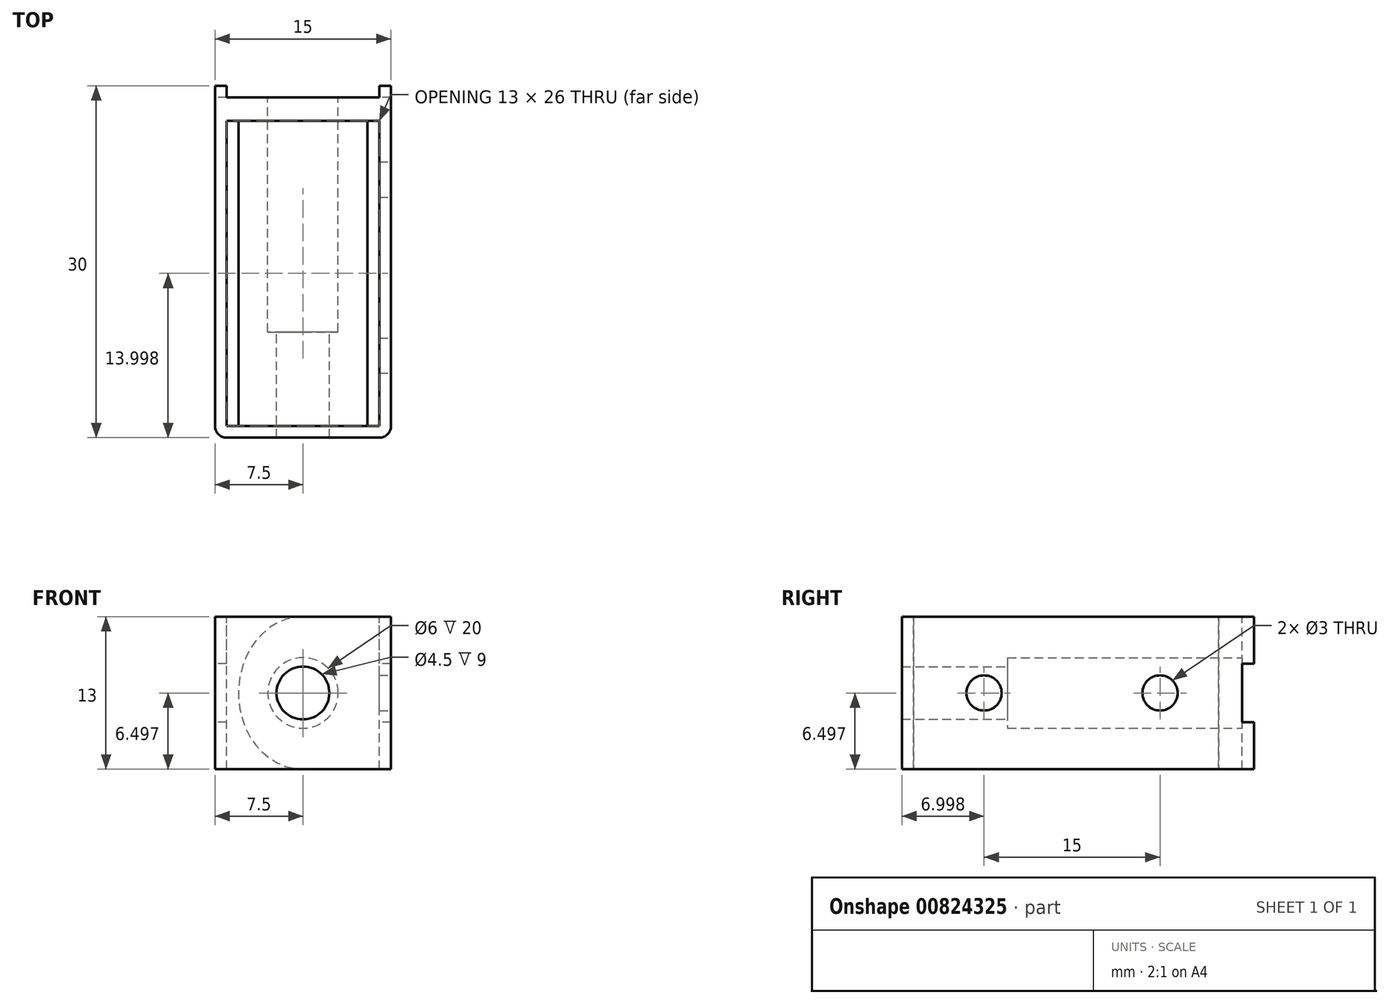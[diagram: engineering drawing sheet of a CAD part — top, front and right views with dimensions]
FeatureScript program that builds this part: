
annotation { "Feature Type Name" : "Feature", "Feature Type Description" : "" }
export const myFeature = defineFeature(function(context is Context, id is Id, definition is map)
    precondition{}
    {
        {
            var Q0;
            Q0=qCreatedBy(makeId("Right.planeOp"),FACE);
            var sketch = newSketch(context, id + "F0", { "sketchPlane" : qUnion([Q0])});
            skLineSegment(sketch, "E0.bottom", {"start": v(-32.8, 20.89) * mm, "end": v(-2.8, 20.89) * mm});
            skLineSegment(sketch, "E0.top", {"start": v(-32.8, 7.89) * mm, "end": v(-2.8, 7.89) * mm});
            skLineSegment(sketch, "E0.left", {"start": v(-32.8, 20.89) * mm, "end": v(-32.8, 7.89) * mm});
            skLineSegment(sketch, "E0.right", {"start": v(-2.8, 20.89) * mm, "end": v(-2.8, 7.89) * mm});
            skSolve(sketch);
        }
        {
            var Q0;
            Q0=makeQuery(id+"F0.imprint","IMPRINT",FACE,{"disambiguationData":[TD([[makeQuery(id+"F0.imprint","IMPRINT",EDGE,{"derivedFrom":sQuery(id+"F0.wireOp",EDGE,"E0.bottom")}),-1.0]])]});
            extrude(context, id + "F1", {"entities" : qUnion([Q0]), "oppositeDirection" : true, "depth" : 15 * mm, "offsetDistance" : 25 * mm});
        }
        {
            var Q0;
            Q0=makeQuery(id+"F1.opExtrude","SWEPT_FACE",FACE,{"disambiguationData":[OSD([sQuery(id+"F0.wireOp",EDGE,"E0.bottom")])]});
            var sketch = newSketch(context, id + "F2", { "sketchPlane" : qUnion([Q0])});
            skLineSegment(sketch, "E1", {"start": v(-1, -31.8) * mm, "end": v(-1, -5.8) * mm});
            skLineSegment(sketch, "E2", {"start": v(-14, -5.8) * mm, "end": v(-14, -31.8) * mm});
            skLineSegment(sketch, "E3", {"start": v(-14, -5.8) * mm, "end": v(-1, -5.8) * mm});
            skLineSegment(sketch, "E4", {"start": v(-14, -31.8) * mm, "end": v(-1, -31.8) * mm});
            skSolve(sketch);
        }
        {
            var Q0;
            Q0 = qSketchRegion(id + "F2", true);
            var Q1;
            Q1=makeQuery(id+"F1.opExtrude","SWEPT_FACE",FACE,{"disambiguationData":[OSD([sQuery(id+"F0.wireOp",EDGE,"E0.top")])]});
            extrude(context, id + "F3", {"entities" : qUnion([Q0]), "operationType" : NewBodyOperationType.REMOVE, "endBound" : BoundingType.UP_TO_SURFACE, "oppositeDirection" : true, "depth" : 25 * mm, "endBoundEntityFace" : qUnion([Q1]), "offsetDistance" : 25 * mm});
        }
        {
            var Q0;
            Q0=makeQuery(id+"F1.opExtrude","CAP_FACE",FACE,{"disambiguationData":[OSD([sQuery(id+"F0.wireOp",EDGE,"E0.bottom"),sQuery(id+"F0.wireOp",EDGE,"E0.top"),sQuery(id+"F0.wireOp",EDGE,"E0.left"),sQuery(id+"F0.wireOp",EDGE,"E0.right")])],"isStart":true});
            var sketch = newSketch(context, id + "F4", { "sketchPlane" : qUnion([Q0])});
            skLineSegment(sketch, "E5.bottom", {"start": v(-25.8, 20.89) * mm, "end": v(-10.8, 20.89) * mm, "construction": true});
            skLineSegment(sketch, "E5.top", {"start": v(-25.8, 7.89) * mm, "end": v(-10.8, 7.89) * mm, "construction": true});
            skLineSegment(sketch, "E5.left", {"start": v(-25.8, 20.89) * mm, "end": v(-25.8, 7.89) * mm, "construction": true});
            skLineSegment(sketch, "E5.right", {"start": v(-10.8, 20.89) * mm, "end": v(-10.8, 7.89) * mm, "construction": true});
            skCircle(sketch, "E6", {"center": v(-25.8, 14.39) * mm, "radius": 1.5 * mm});
            skCircle(sketch, "E7", {"center": v(-10.8, 14.39) * mm, "radius": 1.5 * mm});
            skLineSegment(sketch, "E8", {"start": v(-25.8, 15.89) * mm, "end": v(-10.8, 15.89) * mm, "construction": true});
            skLineSegment(sketch, "E9", {"start": v(-25.8, 12.89) * mm, "end": v(-10.8, 12.89) * mm, "construction": true});
            skSolve(sketch);
        }
        {
            var Q0;
            Q0 = qSketchRegion(id + "F4", true);
            var Q1;
            Q1=makeQuery(id+"F3.boolean.opBoolean","COPY",FACE,{"derivedFrom":makeQuery(id+"F3.opExtrude","SWEPT_FACE",FACE,{"disambiguationData":[OSD([sQuery(id+"F2.wireOp",EDGE,"E1")])]})});
            extrude(context, id + "F5", {"entities" : qUnion([Q0]), "operationType" : NewBodyOperationType.REMOVE, "endBound" : BoundingType.UP_TO_SURFACE, "oppositeDirection" : true, "depth" : 1 * mm, "endBoundEntityFace" : qUnion([Q1]), "offsetDistance" : 25 * mm});
        }
        {
            var Q0;
            Q0=makeQuery(id+"F3.boolean.opBoolean","COPY",FACE,{"derivedFrom":makeQuery(id+"F3.opExtrude","SWEPT_FACE",FACE,{"disambiguationData":[OSD([sQuery(id+"F2.wireOp",EDGE,"E3")])]})});
            var sketch = newSketch(context, id + "F6", { "sketchPlane" : qUnion([Q0])});
            skLineSegment(sketch, "E10.bottom", {"start": v(-0.5, 21.89) * mm, "end": v(-14.5, 21.89) * mm, "construction": true});
            skLineSegment(sketch, "E10.top", {"start": v(-0.5, 6.89) * mm, "end": v(-14.5, 6.89) * mm, "construction": true});
            skLineSegment(sketch, "E10.left", {"start": v(-0.5, 21.89) * mm, "end": v(-0.5, 6.89) * mm, "construction": true});
            skLineSegment(sketch, "E10.right", {"start": v(-14.5, 21.89) * mm, "end": v(-14.5, 6.89) * mm, "construction": true});
            skPoint(sketch, "E10.middle", {"position": v(-7.5, 14.39) * mm});
            skPoint(sketch, "E10.middle.positionSnap0", {"position": v(-1, 14.39) * mm});
            skPoint(sketch, "E10.middle.positionSnap1", {"position": v(-7.5, 20.89) * mm});
            skPoint(sketch, "E10.centerSnap0", {"position": v(-1, 14.39) * mm});
            skPoint(sketch, "E10.centerSnap1", {"position": v(-7.5, 20.89) * mm});
            skLineSegment(sketch, "E11", {"start": v(-7.5, 21.89) * mm, "end": v(-7.5, 6.89) * mm, "construction": true});
            skLineSegment(sketch, "E12", {"start": v(-14.5, 14.39) * mm, "end": v(-0.5, 14.39) * mm, "construction": true});
            skEllipse(sketch, "E13", {"center": v(-7.5, 14.39) * mm, "majorRadius": 6.5 * mm, "minorRadius": 5.5 * mm, "majorAxis": v(0, 1)});
            skSolve(sketch);
        }
        {
            var Q0;
            {var subQ0=sQuery(id+"F6.wireOp",EDGE,"E13");var subQ1=makeQuery(id+"F3.boolean.opBoolean","COPY",EDGE,{"derivedFrom":makeQuery(id+"F3.opExtrude","CAP_EDGE",EDGE,{"disambiguationData":[OSD([sQuery(id+"F2.wireOp",EDGE,"E3")])],"isStart":true})});var subQ2=makeQuery(id+"F6.imprint","INTERSECT",VERTEX,{"disambiguationData":[OD(0.0)],"derivedFrom":[subQ1,subQ0]});Q0=makeQuery(id+"F6.imprint","IMPRINT",FACE,{"disambiguationData":[TD([[makeQuery(id+"F6.imprint","IMPRINT",EDGE,{"disambiguationData":[TD([[subQ2,-1.0]])],"derivedFrom":subQ0}),1.0]])]});}
            var Q1;
            {var subQ0=sQuery(id+"F6.wireOp",EDGE,"E13");var subQ1=makeQuery(id+"F3.boolean.opBoolean","COPY",EDGE,{"derivedFrom":makeQuery(id+"F3.opExtrude","TWEAK_EDGE",EDGE,{"derivedFrom":[makeQuery(id+"F1.opExtrude","SWEPT_FACE",FACE,{"disambiguationData":[OSD([sQuery(id+"F0.wireOp",EDGE,"E0.top")])]}),makeQuery(id+"F2.imprint","IMPRINT",EDGE,{"derivedFrom":sQuery(id+"F2.wireOp",EDGE,"E3")})]})});var subQ2=makeQuery(id+"F6.imprint","INTERSECT",VERTEX,{"disambiguationData":[OD(0.0)],"derivedFrom":[subQ1,subQ0]});Q1=makeQuery(id+"F6.imprint","IMPRINT",FACE,{"disambiguationData":[TD([[makeQuery(id+"F6.imprint","IMPRINT",EDGE,{"disambiguationData":[TD([[subQ2,-1.0]])],"derivedFrom":subQ0}),1.0]])]});}
            var Q2;
            {var subQ0=sQuery(id+"F6.wireOp",EDGE,"E13");var subQ1=makeQuery(id+"F3.boolean.opBoolean","COPY",EDGE,{"derivedFrom":makeQuery(id+"F3.opExtrude","CAP_EDGE",EDGE,{"disambiguationData":[OSD([sQuery(id+"F2.wireOp",EDGE,"E3")])],"isStart":true})});var subQ2=makeQuery(id+"F6.imprint","INTERSECT",VERTEX,{"disambiguationData":[OD(0.0)],"derivedFrom":[subQ1,subQ0]});Q2=makeQuery(id+"F6.imprint","IMPRINT",FACE,{"disambiguationData":[TD([[makeQuery(id+"F6.imprint","IMPRINT",EDGE,{"disambiguationData":[TD([[subQ2,1.0]])],"derivedFrom":subQ0}),1.0]])]});}
            var Q3;
            Q3=makeQuery(id+"F3.boolean.opBoolean","COPY",FACE,{"derivedFrom":makeQuery(id+"F3.opExtrude","SWEPT_FACE",FACE,{"disambiguationData":[OSD([sQuery(id+"F2.wireOp",EDGE,"E4")])]})});
            extrude(context, id + "F7", {"entities" : qUnion([Q0, Q1, Q2]), "operationType" : NewBodyOperationType.ADD, "endBound" : BoundingType.UP_TO_SURFACE, "depth" : 25 * mm, "endBoundEntityFace" : qUnion([Q3]), "offsetDistance" : 25 * mm});
        }
        {
            var Q0;
            Q0=makeQuery(id+"F1.opExtrude","CAP_EDGE",EDGE,{"disambiguationData":[OSD([sQuery(id+"F0.wireOp",EDGE,"E0.left")])],"isStart":false});
            var Q1;
            Q1=makeQuery(id+"F1.opExtrude","CAP_EDGE",EDGE,{"disambiguationData":[OSD([sQuery(id+"F0.wireOp",EDGE,"E0.left")])],"isStart":true});
            fillet(context, id + "F8", {"entities" : qUnion([Q0, Q1]), "radius" : 1 * mm, "tangentPropagation" : true, "allowEdgeOverflow" : false});
        }
        {
            var Q0;
            Q0=makeQuery(id+"F1.opExtrude","SWEPT_FACE",FACE,{"disambiguationData":[OSD([sQuery(id+"F0.wireOp",EDGE,"E0.right")])]});
            var sketch = newSketch(context, id + "F9", { "sketchPlane" : qUnion([Q0])});
            skLineSegment(sketch, "E14.bottom", {"start": v(14, 7.89) * mm, "end": v(1, 7.89) * mm});
            skLineSegment(sketch, "E14.top", {"start": v(14, 20.89) * mm, "end": v(1, 20.89) * mm});
            skLineSegment(sketch, "E14.left", {"start": v(14, 7.89) * mm, "end": v(14, 20.89) * mm});
            skLineSegment(sketch, "E14.right", {"start": v(1, 7.89) * mm, "end": v(1, 20.89) * mm});
            skPoint(sketch, "E14.middle", {"position": v(7.5, 14.39) * mm});
            skPoint(sketch, "E14.middle.positionSnap0", {"position": v(15, 14.39) * mm});
            skPoint(sketch, "E14.middle.positionSnap1", {"position": v(7.5, 20.89) * mm});
            skPoint(sketch, "E14.centerSnap0", {"position": v(15, 14.39) * mm});
            skPoint(sketch, "E14.centerSnap1", {"position": v(7.5, 20.89) * mm});
            skLineSegment(sketch, "E15.bottom", {"start": v(0, 16.89) * mm, "end": v(15, 16.89) * mm});
            skLineSegment(sketch, "E15.top", {"start": v(0, 11.89) * mm, "end": v(15, 11.89) * mm});
            skLineSegment(sketch, "E15.left", {"start": v(0, 16.89) * mm, "end": v(0, 11.89) * mm});
            skLineSegment(sketch, "E15.right", {"start": v(15, 16.89) * mm, "end": v(15, 11.89) * mm});
            skSolve(sketch);
        }
        {
            var Q0;
            Q0 = qSketchRegion(id + "F9", true);
            extrude(context, id + "F10", {"entities" : qUnion([Q0]), "operationType" : NewBodyOperationType.REMOVE, "oppositeDirection" : true, "depth" : 1 * mm, "offsetDistance" : 25 * mm});
        }
        {
            var Q0;
            Q0=makeQuery(id+"F10.boolean.opBoolean","COPY",FACE,{"derivedFrom":makeQuery(id+"F10.opExtrude","CAP_FACE",FACE,{"disambiguationData":[OSD([sQuery(id+"F9.wireOp",EDGE,"E14.bottom"),sQuery(id+"F9.wireOp",EDGE,"E14.top"),sQuery(id+"F9.wireOp",EDGE,"E14.left"),sQuery(id+"F9.wireOp",EDGE,"E14.right"),sQuery(id+"F9.wireOp",EDGE,"E15.bottom"),sQuery(id+"F9.wireOp",EDGE,"E15.top"),sQuery(id+"F9.wireOp",EDGE,"E15.left"),sQuery(id+"F9.wireOp",EDGE,"E15.right")])],"isStart":false})});
            var sketch = newSketch(context, id + "F11", { "sketchPlane" : qUnion([Q0])});
            skCircle(sketch, "E16", {"center": v(7.5, 14.39) * mm, "radius": 3 * mm});
            skPoint(sketch, "E16.centerSnap0", {"position": v(7.5, 20.89) * mm});
            skPoint(sketch, "E16.centerSnap1", {"position": v(0, 14.39) * mm});
            skSolve(sketch);
        }
        {
            var Q0;
            Q0 = qSketchRegion(id + "F11", true);
            var Q1;
            {var subQ0=sQuery(id+"F2.wireOp",EDGE,"E1");var subQ1=sQuery(id+"F2.wireOp",EDGE,"E4");var subQ2=sQuery(id+"F6.wireOp",EDGE,"E13");var subQ3=sQuery(id+"F2.wireOp",EDGE,"E3");var subQ4=makeQuery(id+"F3.boolean.opBoolean","COPY",EDGE,{"derivedFrom":makeQuery(id+"F3.opExtrude","CAP_EDGE",EDGE,{"disambiguationData":[OSD([subQ3])],"isStart":true})});var subQ5=makeQuery(id+"F6.imprint","INTERSECT",VERTEX,{"disambiguationData":[OD(0.0)],"derivedFrom":[subQ4,subQ2]});var subQ6=makeQuery(id+"F6.imprint","INTERSECT",VERTEX,{"disambiguationData":[OD(1.0)],"derivedFrom":[subQ4,subQ2]});Q1=makeQuery(id+"F7.boolean.opBoolean","SPLIT",FACE,{"disambiguationData":[TD([makeQuery(id+"F1.opExtrude","SWEPT_FACE",FACE,{"disambiguationData":[OSD([sQuery(id+"F0.wireOp",EDGE,"E0.bottom")])]}),makeQuery(id+"F3.boolean.opBoolean","COPY",FACE,{"derivedFrom":makeQuery(id+"F3.opExtrude","SWEPT_FACE",FACE,{"disambiguationData":[OSD([subQ0])]})}),makeQuery(id+"F7.opExtrude","CAP_FACE",FACE,{"disambiguationData":[OSD([subQ1])],"isStart":false}),makeQuery(id+"F7.opExtrude","SWEPT_FACE",FACE,{"disambiguationData":[OSD([subQ2]),TDD([makeQuery(id+"F6.imprint","IMPRINT",EDGE,{"disambiguationData":[TD([[subQ5,-1.0]])],"derivedFrom":subQ2}),makeQuery(id+"F6.imprint","IMPRINT",EDGE,{"disambiguationData":[TD([[subQ6,1.0]])],"derivedFrom":subQ2}),makeQuery(id+"F6.imprint","IMPRINT",EDGE,{"disambiguationData":[TD([[subQ5,1.0]])],"derivedFrom":subQ2})])]})])],"derivedFrom":makeQuery(id+"F3.boolean.opBoolean","COPY",FACE,{"derivedFrom":makeQuery(id+"F3.opExtrude","SWEPT_FACE",FACE,{"disambiguationData":[OSD([subQ1])]})})});}
            extrude(context, id + "F12", {"entities" : qUnion([Q0]), "operationType" : NewBodyOperationType.REMOVE, "oppositeDirection" : true, "depth" : 20 * mm, "endBoundEntityFace" : qUnion([Q1]), "offsetDistance" : 25 * mm});
        }
        {
            var Q0;
            Q0=makeQuery(id+"F12.boolean.opBoolean","COPY",FACE,{"derivedFrom":makeQuery(id+"F12.opExtrude","CAP_FACE",FACE,{"disambiguationData":[OSD([sQuery(id+"F11.wireOp",EDGE,"E16")])],"isStart":false})});
            var sketch = newSketch(context, id + "F13", { "sketchPlane" : qUnion([Q0])});
            skCircle(sketch, "E17", {"center": v(7.5, 14.39) * mm, "radius": 2.25 * mm});
            skSolve(sketch);
        }
        {
            var Q0;
            Q0=makeQuery(id+"F13.imprint","IMPRINT",FACE,{"disambiguationData":[TD([[makeQuery(id+"F13.imprint","IMPRINT",EDGE,{"derivedFrom":sQuery(id+"F13.wireOp",EDGE,"E17")}),1.0]])]});
            var Q1;
            Q1=makeQuery(id+"F1.opExtrude","SWEPT_FACE",FACE,{"disambiguationData":[OSD([sQuery(id+"F0.wireOp",EDGE,"E0.left")])]});
            extrude(context, id + "F14", {"entities" : qUnion([Q0]), "operationType" : NewBodyOperationType.REMOVE, "endBound" : BoundingType.UP_TO_SURFACE, "oppositeDirection" : true, "depth" : 25 * mm, "endBoundEntityFace" : qUnion([Q1]), "offsetDistance" : 25 * mm});
        }
    });
